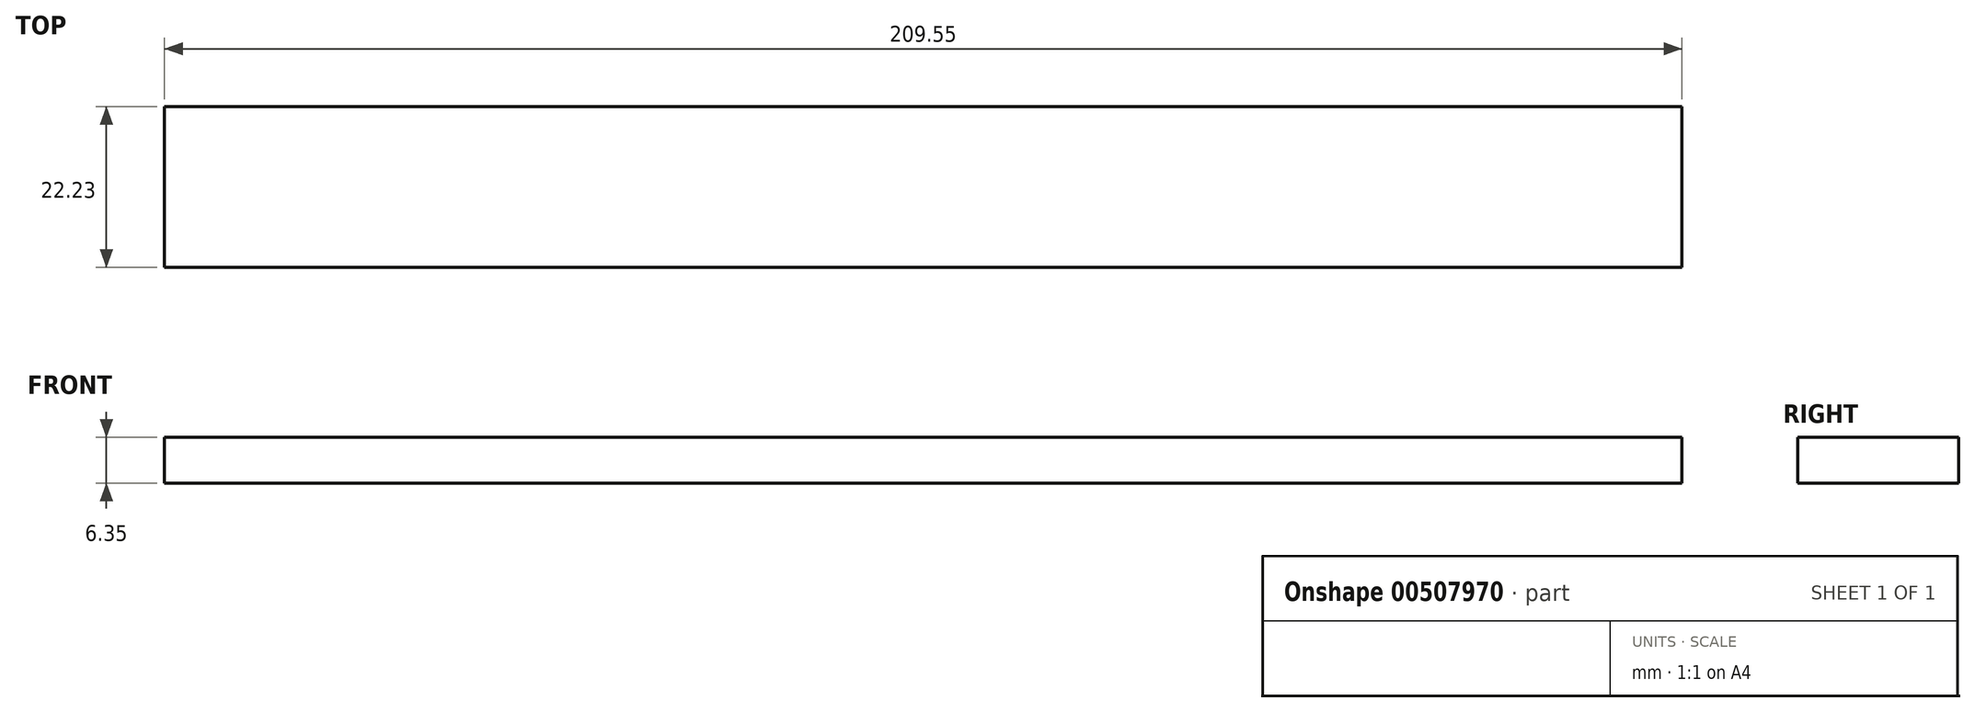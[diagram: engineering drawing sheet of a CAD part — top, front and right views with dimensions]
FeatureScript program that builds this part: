
annotation { "Feature Type Name" : "Feature", "Feature Type Description" : "" }
export const myFeature = defineFeature(function(context is Context, id is Id, definition is map)
    precondition{}
    {
        {
            var Q0;
            Q0=qCreatedBy(makeId("Top.planeOp"),FACE);
            var sketch = newSketch(context, id + "F0", { "sketchPlane" : qUnion([Q0])});
            skLineSegment(sketch, "E0.bottom", {"start": v(0, 0) * mm, "end": v(209.55, 0) * mm});
            skLineSegment(sketch, "E0.top", {"start": v(0, -22.22) * mm, "end": v(209.55, -22.22) * mm});
            skLineSegment(sketch, "E0.left", {"start": v(0, 0) * mm, "end": v(0, -22.22) * mm});
            skLineSegment(sketch, "E0.right", {"start": v(209.55, 0) * mm, "end": v(209.55, -22.22) * mm});
            skSolve(sketch);
        }
        {
            var Q0;
            Q0=makeQuery(id+"F0.imprint","IMPRINT",FACE,{"disambiguationData":[TD([[makeQuery(id+"F0.imprint","IMPRINT",EDGE,{"derivedFrom":sQuery(id+"F0.wireOp",EDGE,"E0.bottom")}),-1.0]])]});
            extrude(context, id + "F1", {"entities" : qUnion([Q0]), "depth" : 6.35 * mm, "offsetDistance" : 25.4 * mm});
        }
    });
